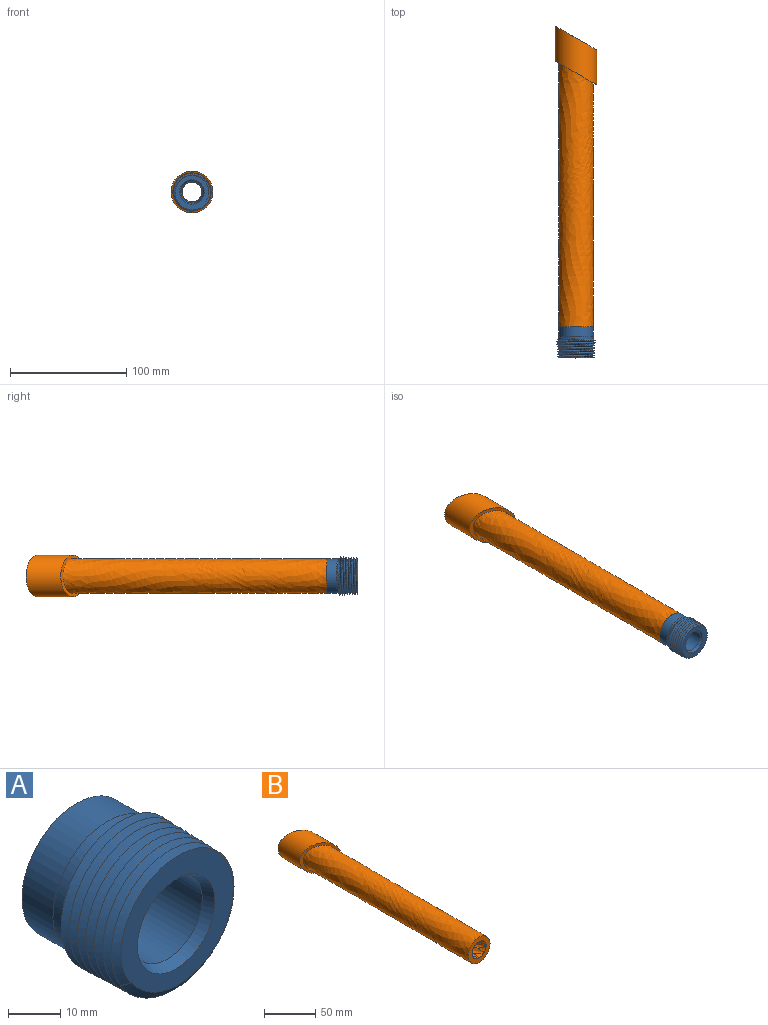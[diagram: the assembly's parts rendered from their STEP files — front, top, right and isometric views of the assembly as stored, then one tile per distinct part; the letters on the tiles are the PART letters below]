
ASSEMBLY  parts=2 mates=1
PART A: 13 faces, bbox 42.6x40.5x42.6 mm
  f0: cylinder r=14.87mm len=29.74mm, axis (0,-1,0), area 785.1mm2, adj f7,f10
  f1: cone r=14.87mm half-angle=1.6deg, axis (0,1,0), area 0.6mm2, adj f3,f5,f9
  f2: torus R=51.79mm, axis (0,-1,0), area 166.7mm2, adj f9,f11
  f3: bspline ~33.3x33.19mm, area 1452mm2, adj f1,f4,f7,f8,f9,f12
  f4: bspline ~33.24x33.19mm, area 1479.1mm2, adj f3,f6,f7,f9,f12
  f5: plane 0.18x0.05mm, normal (-0.71,0,0.71), area 0mm2, adj f1,f6,f8,f9
  f6: plane 0.8x0.67mm, normal (-0.64,0,-0.77), area 0.1mm2, adj f4,f5,f7,f8,f9
  f7: cone r=14.87mm half-angle=1.6deg, axis (0,1,0), area 163.2mm2, adj f0,f3,f4,f6,f12
  f8: plane 0.19x0.17mm, normal (0,-1,0), area 0mm2, adj f3,f5,f6
  f9: plane 30.44x30.41mm, normal (0,-1,0), area 376.2mm2, adj f1,f2,f3,f4,f5,f6
  f10: plane 29.74x29.74mm, normal (0,1,0), area 409.5mm2, adj f0,f11
  f11: cylinder r=9.53mm len=24.57mm, axis (0,1,0), area 1470.2mm2, adj f2,f10
  f12: bspline ~31.39x21.52mm, area 45.7mm2, adj f3,f4,f7
PART B: 23 faces, bbox 67.9x259.3x67.9 mm
  f0: plane 22.89x22.89mm, normal (0,1,0), area 151mm2, adj f1,f2,f3,f4,f5,f6,f7,f8
  f1: bspline ~227.5x19.54mm, area 1615.7mm2, adj f0,f2,f8,f16,f22
  f2: bspline ~227.5x21.56mm, area 1615.7mm2, adj f0,f1,f3,f21,f22
  f3: bspline ~227.5x21.83mm, area 1615.7mm2, adj f0,f2,f4,f20,f21
  f4: bspline ~227.5x21.56mm, area 1615.7mm2, adj f0,f3,f5,f19,f20
  f5: bspline ~227.5x21.83mm, area 1615.7mm2, adj f0,f4,f6,f18,f19
  f6: bspline ~227.5x21.56mm, area 1615.7mm2, adj f0,f5,f7,f17,f18
  f7: bspline ~227.5x21.83mm, area 1615.7mm2, adj f0,f6,f8,f15,f17
  f8: bspline ~227.5x21.56mm, area 1615.7mm2, adj f0,f1,f7,f15,f16
  f9: plane 30x30mm, normal (0,-1,0), area 414.3mm2, adj f10,f15,f16,f17,f18,f19,f20,f21
  f10: bspline ~227.5x67.92mm, area 20601.2mm2, adj f9,f11
  f11: plane 36.02x36.02mm, normal (-0.5,-0.87,0), area 360.6mm2, adj f10,f12
  f12: cylinder r=18.01mm len=50.95mm, axis (0,-1,0), area 3395mm2, adj f11,f14
  f13: cylinder r=11.45mm len=36.7mm, axis (0,-1,0), area 2157.7mm2, adj f0,f14
  f14: plane 36.02x36.02mm, normal (0.5,0.87,0), area 701.5mm2, adj f12,f13
  f15: cone r=9.65mm half-angle=8.2deg, axis (0,-1,0), area 25.6mm2, adj f7,f8,f9
  f16: cone r=9.65mm half-angle=8.2deg, axis (0,-1,0), area 25.6mm2, adj f1,f8,f9
  f17: cone r=9.65mm half-angle=8.2deg, axis (0,-1,0), area 25.6mm2, adj f6,f7,f9
  f18: cone r=9.65mm half-angle=8.2deg, axis (0,-1,0), area 25.6mm2, adj f5,f6,f9
  f19: cone r=9.65mm half-angle=8.2deg, axis (0,-1,0), area 25.6mm2, adj f4,f5,f9
  f20: cone r=9.65mm half-angle=8.2deg, axis (0,-1,0), area 25.6mm2, adj f3,f4,f9
  f21: cone r=9.65mm half-angle=8.2deg, axis (0,-1,0), area 25.6mm2, adj f2,f3,f9
  f22: cone r=9.65mm half-angle=8.2deg, axis (0,-1,0), area 25.6mm2, adj f1,f2,f9
PLACE A rot(axis=(0,1,0),90deg) t=(-31.97,-140,0)mm
PLACE B at identity
MATE fastened A.f1 <-> B.f15  axis (0,1,0) through (0,0,0)mm
